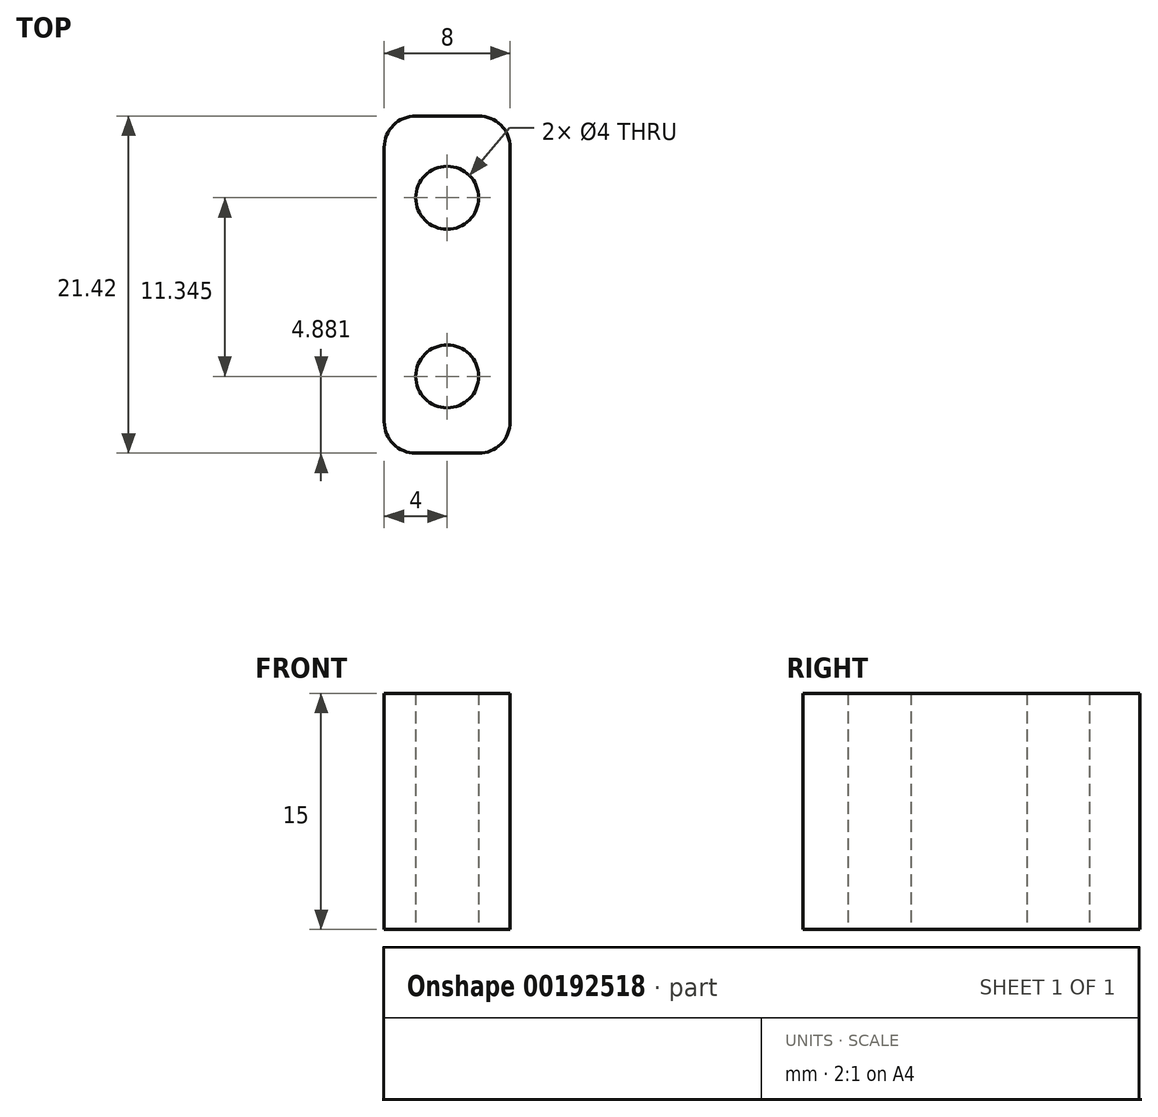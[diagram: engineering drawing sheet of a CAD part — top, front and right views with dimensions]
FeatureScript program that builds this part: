
annotation { "Feature Type Name" : "Feature", "Feature Type Description" : "" }
export const myFeature = defineFeature(function(context is Context, id is Id, definition is map)
    precondition{}
    {
        {
            var Q0;
            Q0=qCreatedBy(makeId("Top.planeOp"),FACE);
            var sketch = newSketch(context, id + "F0", { "sketchPlane" : qUnion([Q0])});
            skLineSegment(sketch, "E0.bottom", {"start": v(-4, -10.66) * mm, "end": v(4, -10.66) * mm});
            skLineSegment(sketch, "E0.top", {"start": v(-4, 10.76) * mm, "end": v(4, 10.76) * mm});
            skLineSegment(sketch, "E0.left", {"start": v(-4, -10.66) * mm, "end": v(-4, 10.76) * mm});
            skLineSegment(sketch, "E0.right", {"start": v(4, -10.66) * mm, "end": v(4, 10.76) * mm});
            skCircle(sketch, "E1", {"center": v(0, 5.57) * mm, "radius": 2 * mm});
            skCircle(sketch, "E2", {"center": v(0, -5.78) * mm, "radius": 2 * mm});
            skSolve(sketch);
        }
        {
            var Q0;
            Q0=makeQuery(id+"F0.imprint","IMPRINT",FACE,{"disambiguationData":[TD([[makeQuery(id+"F0.imprint","IMPRINT",EDGE,{"derivedFrom":sQuery(id+"F0.wireOp",EDGE,"E0.bottom")}),1.0]])]});
            extrude(context, id + "F1", {"entities" : qUnion([Q0]), "flatOperationType" : FlatOperationType.REMOVE, "offsetDistance" : 25 * mm, "depth" : 15 * mm, "domain" : OperationDomain.MODEL});
        }
        {
            var Q0;
            Q0=makeQuery(id+"F1.opExtrude","SWEPT_EDGE",EDGE,{"disambiguationData":[OSD([sQuery(id+"F0.wireOp",EDGE,"E0.bottom"),sQuery(id+"F0.wireOp",EDGE,"E0.left")])]});
            var Q1;
            Q1=makeQuery(id+"F1.opExtrude","SWEPT_EDGE",EDGE,{"disambiguationData":[OSD([sQuery(id+"F0.wireOp",EDGE,"E0.top"),sQuery(id+"F0.wireOp",EDGE,"E0.left")])]});
            var Q2;
            Q2=makeQuery(id+"F1.opExtrude","SWEPT_EDGE",EDGE,{"disambiguationData":[OSD([sQuery(id+"F0.wireOp",EDGE,"E0.bottom"),sQuery(id+"F0.wireOp",EDGE,"E0.right")])]});
            var Q3;
            Q3=makeQuery(id+"F1.opExtrude","SWEPT_EDGE",EDGE,{"disambiguationData":[OSD([sQuery(id+"F0.wireOp",EDGE,"E0.top"),sQuery(id+"F0.wireOp",EDGE,"E0.right")])]});
            fillet(context, id + "F2", {"entities" : qUnion([Q0, Q1, Q2, Q3]), "radius" : 2 * mm, "tangentPropagation" : true, "allowEdgeOverflow" : false});
        }
    });
